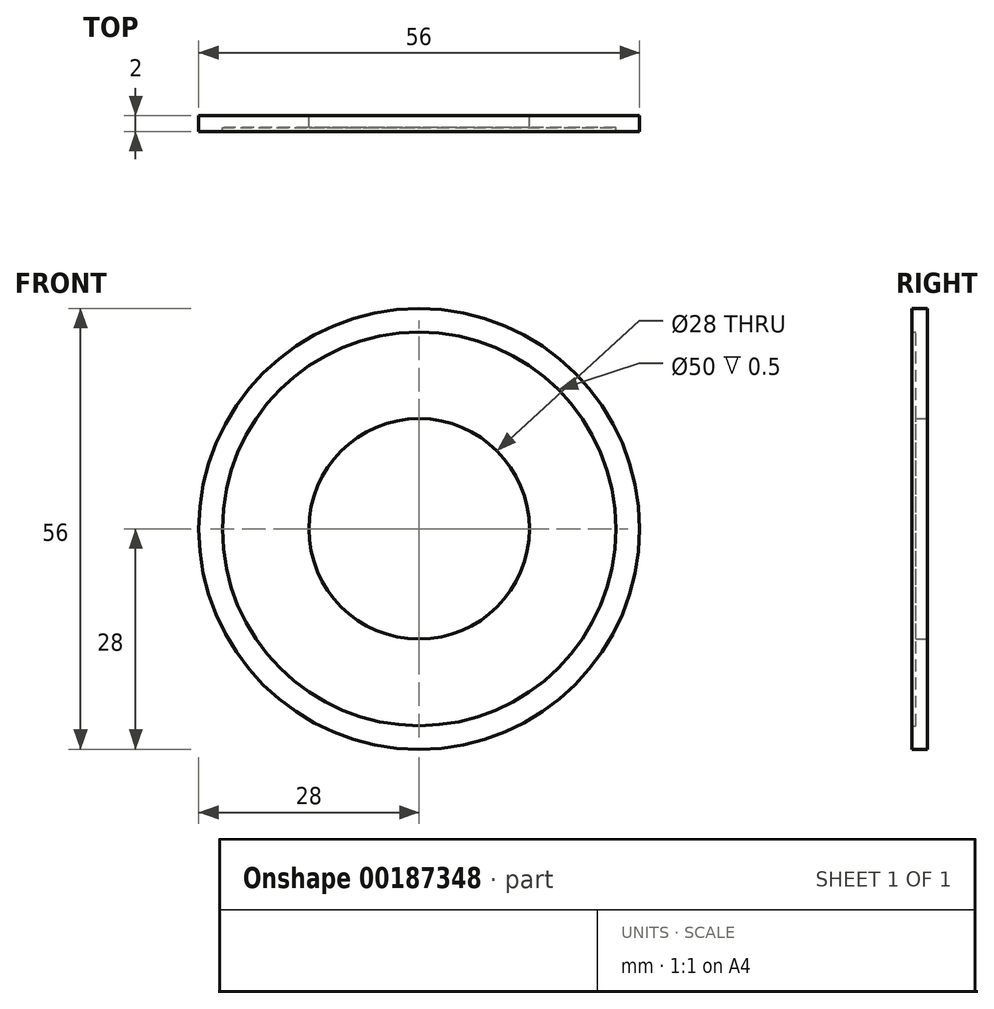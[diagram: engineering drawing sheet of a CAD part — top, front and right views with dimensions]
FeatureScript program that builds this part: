
annotation { "Feature Type Name" : "Feature", "Feature Type Description" : "" }
export const myFeature = defineFeature(function(context is Context, id is Id, definition is map)
    precondition{}
    {
        {
            var Q0;
            Q0=qCreatedBy(makeId("Front.planeOp"),FACE);
            var sketch = newSketch(context, id + "F0", { "sketchPlane" : qUnion([Q0])});
            skCircle(sketch, "E0", {"center": v(0, 0) * mm, "radius": 28 * mm});
            skCircle(sketch, "E1", {"center": v(0, 0) * mm, "radius": 25 * mm});
            skCircle(sketch, "E2", {"center": v(0, 0) * mm, "radius": 14 * mm});
            skSolve(sketch);
        }
        {
            var Q0;
            Q0=makeQuery(id+"F0.imprint","IMPRINT",FACE,{"disambiguationData":[TD([[makeQuery(id+"F0.imprint","IMPRINT",EDGE,{"derivedFrom":sQuery(id+"F0.wireOp",EDGE,"E0")}),1.0]])]});
            var Q1;
            Q1=makeQuery(id+"F0.imprint","IMPRINT",FACE,{"disambiguationData":[TD([[makeQuery(id+"F0.imprint","IMPRINT",EDGE,{"derivedFrom":sQuery(id+"F0.wireOp",EDGE,"E1")}),1.0]])]});
            extrude(context, id + "F1", {"entities" : qUnion([Q0, Q1]), "depth" : 1.5 * mm});
        }
        {
            var Q0;
            Q0=qSketchRegion(id+"F0",true);
            extrude(context, id + "F2", {"entities" : qUnion([Q0]), "operationType" : NewBodyOperationType.ADD, "depth" : 2 * mm});
        }
    });
